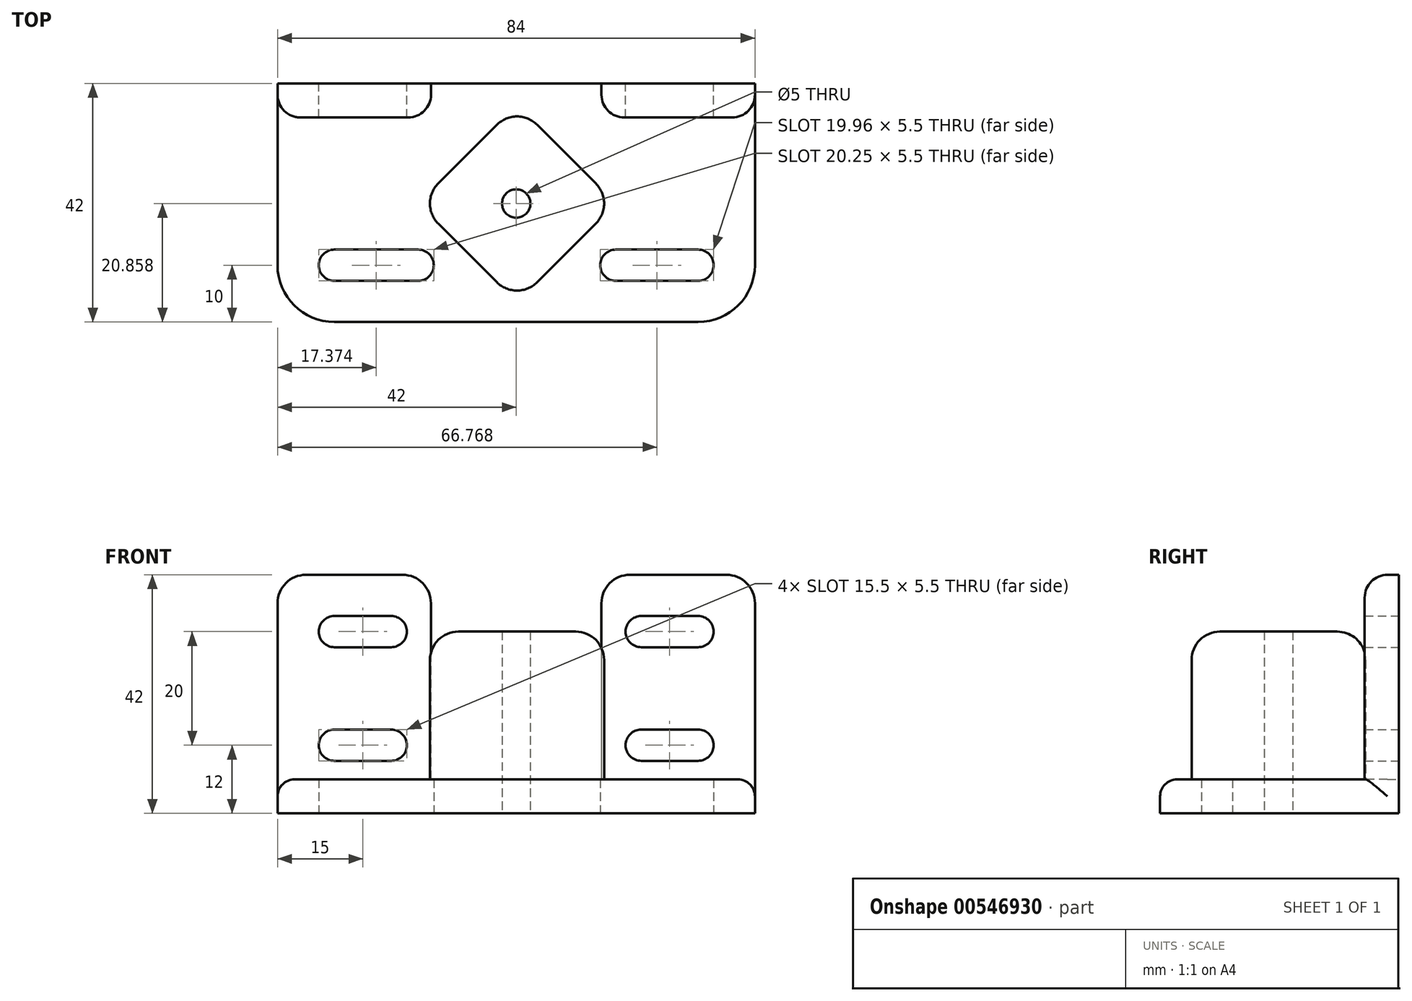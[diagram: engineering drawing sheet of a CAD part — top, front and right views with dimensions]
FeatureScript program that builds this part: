
annotation { "Feature Type Name" : "Feature", "Feature Type Description" : "" }
export const myFeature = defineFeature(function(context is Context, id is Id, definition is map)
    precondition{}
    {
        {
            var Q0;
            Q0=qCreatedBy(makeId("Top.planeOp"),FACE);
            var sketch = newSketch(context, id + "F0", { "sketchPlane" : qUnion([Q0])});
            skLineSegment(sketch, "E0", {"start": v(0, 0) * mm, "end": v(0, -32) * mm});
            skLineSegment(sketch, "E1", {"start": v(10, -42) * mm, "end": v(74, -42) * mm});
            skLineSegment(sketch, "E2", {"start": v(84, -32) * mm, "end": v(84, 0) * mm});
            skLineSegment(sketch, "E3", {"start": v(84, 0) * mm, "end": v(0, 0) * mm});
            skLineSegment(sketch, "E4.0", {"start": v(84.14, -21.14) * mm, "end": v(59.54, -21.14) * mm, "construction": true});
            skLineSegment(sketch, "E5.0", {"start": v(42, 0) * mm, "end": v(42, -42) * mm, "construction": true});
            skLineSegment(sketch, "E6.0", {"start": v(59.54, -21.14) * mm, "end": v(42.14, -3.75) * mm});
            skLineSegment(sketch, "E7.0", {"start": v(42.14, -38.54) * mm, "end": v(24.75, -21.14) * mm});
            skLineSegment(sketch, "E8.0", {"start": v(42.14, -3.75) * mm, "end": v(24.75, -21.14) * mm});
            skLineSegment(sketch, "E9.0", {"start": v(59.54, -21.14) * mm, "end": v(42.14, -38.54) * mm});
            skLineSegment(sketch, "E10.trimOffspring", {"start": v(24.75, -21.14) * mm, "end": v(0.14, -21.14) * mm, "construction": true});
            skLineSegment(sketch, "E11", {"start": v(24.75, 0) * mm, "end": v(24.75, -42) * mm, "construction": true});
            skLineSegment(sketch, "E12", {"start": v(59.54, 0) * mm, "end": v(59.54, -42) * mm, "construction": true});
            skLineSegment(sketch, "E13.0", {"start": v(74, -10) * mm, "end": v(59.54, -10) * mm, "construction": true});
            skLineSegment(sketch, "E14.0", {"start": v(10, -32) * mm, "end": v(24.75, -32) * mm, "construction": true});
            skLineSegment(sketch, "E15.0", {"start": v(10, 0) * mm, "end": v(10, -42) * mm, "construction": true});
            skLineSegment(sketch, "E16.0", {"start": v(74, -42) * mm, "end": v(74, 0) * mm, "construction": true});
            skLineSegment(sketch, "E17.trimOffspring", {"start": v(24.75, -10) * mm, "end": v(10, -10) * mm, "construction": true});
            skLineSegment(sketch, "E18.trimOffspring", {"start": v(59.54, -32) * mm, "end": v(74, -32) * mm, "construction": true});
            skArc(sketch, "E19", {"start": v(10, -29.25) * mm, "mid": v(7.25, -32) * mm, "end": v(10, -34.75) * mm});
            skArc(sketch, "E20", {"start": v(24.75, -34.75) * mm, "mid": v(27.5, -32) * mm, "end": v(24.75, -29.25) * mm});
            skArc(sketch, "E21", {"start": v(59.54, -29.25) * mm, "mid": v(56.79, -32) * mm, "end": v(59.54, -34.75) * mm});
            skArc(sketch, "E22", {"start": v(74, -34.75) * mm, "mid": v(76.75, -32) * mm, "end": v(74, -29.25) * mm});
            skLineSegment(sketch, "E23", {"start": v(10, -29.25) * mm, "end": v(24.75, -29.25) * mm});
            skLineSegment(sketch, "E24", {"start": v(24.75, -34.75) * mm, "end": v(10, -34.75) * mm});
            skLineSegment(sketch, "E25", {"start": v(59.54, -29.25) * mm, "end": v(74, -29.25) * mm});
            skLineSegment(sketch, "E26", {"start": v(74, -34.75) * mm, "end": v(59.54, -34.75) * mm});
            skPoint(sketch, "E27.visualSharp", {"position": v(0, 0) * mm});
            skPoint(sketch, "E28.visualSharp", {"position": v(0, -42) * mm});
            skArc(sketch, "E28.filletArc", {"start": v(0, -32) * mm, "mid": v(2.93, -39.07) * mm, "end": v(10, -42) * mm});
            skPoint(sketch, "E29.visualSharp", {"position": v(84, -42) * mm});
            skArc(sketch, "E29.filletArc", {"start": v(74, -42) * mm, "mid": v(81.07, -39.07) * mm, "end": v(84, -32) * mm});
            skPoint(sketch, "E30.visualSharp", {"position": v(84, 0) * mm});
            skLineSegment(sketch, "E31", {"start": v(24.75, -21.14) * mm, "end": v(42, -21.14) * mm, "construction": true});
            skCircle(sketch, "E32", {"center": v(42, -21.14) * mm, "radius": 2.5 * mm});
            skSolve(sketch);
        }
        {
            var Q0;
            Q0=makeQuery(id+"F0.imprint","IMPRINT",FACE,{"disambiguationData":[TD([[makeQuery(id+"F0.imprint","IMPRINT",EDGE,{"derivedFrom":sQuery(id+"F0.wireOp",EDGE,"E0")}),1.0]])]});
            extrude(context, id + "F1", {"entities" : qUnion([Q0]), "depth" : 6 * mm, "offsetDistance" : 25 * mm});
        }
        {
            var Q0;
            Q0=makeQuery(id+"F0.imprint","IMPRINT",FACE,{"disambiguationData":[TD([[makeQuery(id+"F0.imprint","IMPRINT",EDGE,{"derivedFrom":sQuery(id+"F0.wireOp",EDGE,"E6.0")}),1.0]])]});
            extrude(context, id + "F2", {"entities" : qUnion([Q0]), "operationType" : NewBodyOperationType.ADD, "depth" : 32 * mm, "offsetDistance" : 25 * mm});
        }
        {
            var Q0;
            Q0=makeQuery(id+"F2.opExtrude","SWEPT_EDGE",EDGE,{"disambiguationData":[OSD([sQuery(id+"F0.wireOp",EDGE,"E7.0"),sQuery(id+"F0.wireOp",EDGE,"E9.0")])]});
            var Q1;
            Q1=makeQuery(id+"F2.opExtrude","SWEPT_EDGE",EDGE,{"disambiguationData":[OSD([sQuery(id+"F0.wireOp",EDGE,"E7.0"),sQuery(id+"F0.wireOp",EDGE,"E8.0")])]});
            var Q2;
            Q2=makeQuery(id+"F2.opExtrude","SWEPT_EDGE",EDGE,{"disambiguationData":[OSD([sQuery(id+"F0.wireOp",EDGE,"E6.0"),sQuery(id+"F0.wireOp",EDGE,"E9.0")])]});
            var Q3;
            Q3=makeQuery(id+"F2.opExtrude","SWEPT_EDGE",EDGE,{"disambiguationData":[OSD([sQuery(id+"F0.wireOp",EDGE,"E6.0"),sQuery(id+"F0.wireOp",EDGE,"E8.0")])]});
            var Q4;
            Q4=makeQuery(id+"F2.opExtrude","CAP_EDGE",EDGE,{"disambiguationData":[OSD([sQuery(id+"F0.wireOp",EDGE,"E8.0")])],"isStart":false});
            var Q5;
            Q5=makeQuery(id+"F2.opExtrude","CAP_EDGE",EDGE,{"disambiguationData":[OSD([sQuery(id+"F0.wireOp",EDGE,"E6.0")])],"isStart":false});
            var Q6;
            Q6=makeQuery(id+"F2.opExtrude","CAP_EDGE",EDGE,{"disambiguationData":[OSD([sQuery(id+"F0.wireOp",EDGE,"E9.0")])],"isStart":false});
            var Q7;
            Q7=makeQuery(id+"F2.opExtrude","CAP_EDGE",EDGE,{"disambiguationData":[OSD([sQuery(id+"F0.wireOp",EDGE,"E7.0")])],"isStart":false});
            fillet(context, id + "F3", {"entities" : qUnion([Q0, Q1, Q2, Q3, Q4, Q5, Q6, Q7]), "radius" : 5 * mm, "tangentPropagation" : true, "allowEdgeOverflow" : false});
        }
        {
            var Q0;
            Q0=makeQuery(id+"F1.opExtrude","CAP_EDGE",EDGE,{"disambiguationData":[OSD([sQuery(id+"F0.wireOp",EDGE,"E1")])],"isStart":false});
            fillet(context, id + "F4", {"entities" : qUnion([Q0]), "radius" : 3 * mm, "tangentPropagation" : true, "allowEdgeOverflow" : false});
        }
        {
            var Q0;
            Q0=qCreatedBy(makeId("Front.planeOp"),FACE);
            var sketch = newSketch(context, id + "F5", { "sketchPlane" : qUnion([Q0])});
            skLineSegment(sketch, "E33", {"start": v(0, 0) * mm, "end": v(0, 37) * mm});
            skLineSegment(sketch, "E34", {"start": v(5, 42) * mm, "end": v(22, 42) * mm});
            skLineSegment(sketch, "E35", {"start": v(84, 37) * mm, "end": v(84, 0) * mm});
            skLineSegment(sketch, "E36.0", {"start": v(10, 32) * mm, "end": v(20, 32) * mm, "construction": true});
            skLineSegment(sketch, "E37.0", {"start": v(10, 9.25) * mm, "end": v(10, 14.75) * mm, "construction": true});
            skLineSegment(sketch, "E38.0", {"start": v(74, 34.75) * mm, "end": v(74, 29.25) * mm, "construction": true});
            skLineSegment(sketch, "E39.0", {"start": v(20, 9.25) * mm, "end": v(20, 14.75) * mm, "construction": true});
            skLineSegment(sketch, "E40.0", {"start": v(64, 34.75) * mm, "end": v(64, 29.25) * mm, "construction": true});
            skLineSegment(sketch, "E41.trimOffspring", {"start": v(62, 42) * mm, "end": v(79, 42) * mm});
            skPoint(sketch, "E42.visualSharp", {"position": v(0, 42) * mm});
            skArc(sketch, "E42.filletArc", {"start": v(5, 42) * mm, "mid": v(1.46, 40.54) * mm, "end": v(0, 37) * mm});
            skPoint(sketch, "E43.visualSharp", {"position": v(84, 42) * mm});
            skArc(sketch, "E43.filletArc", {"start": v(84, 37) * mm, "mid": v(82.54, 40.54) * mm, "end": v(79, 42) * mm});
            skLineSegment(sketch, "E44.trimOffspring", {"start": v(64, 32) * mm, "end": v(74, 32) * mm, "construction": true});
            skArc(sketch, "E45", {"start": v(20, 29.25) * mm, "mid": v(22.75, 32) * mm, "end": v(20, 34.75) * mm});
            skArc(sketch, "E46", {"start": v(10, 34.75) * mm, "mid": v(7.25, 32) * mm, "end": v(10, 29.25) * mm});
            skArc(sketch, "E47", {"start": v(64, 34.75) * mm, "mid": v(61.25, 32) * mm, "end": v(64, 29.25) * mm});
            skArc(sketch, "E48", {"start": v(74, 29.25) * mm, "mid": v(76.75, 32) * mm, "end": v(74, 34.75) * mm});
            skLineSegment(sketch, "E49.0", {"start": v(10, 12) * mm, "end": v(20, 12) * mm, "construction": true});
            skLineSegment(sketch, "E50.0", {"start": v(64, 12) * mm, "end": v(74, 12) * mm, "construction": true});
            skArc(sketch, "E51", {"start": v(10, 14.75) * mm, "mid": v(7.25, 12) * mm, "end": v(10, 9.25) * mm});
            skArc(sketch, "E52", {"start": v(20, 9.25) * mm, "mid": v(22.75, 12) * mm, "end": v(20, 14.75) * mm});
            skArc(sketch, "E53", {"start": v(64, 14.75) * mm, "mid": v(61.25, 12) * mm, "end": v(64, 9.25) * mm});
            skArc(sketch, "E54", {"start": v(74, 9.25) * mm, "mid": v(76.75, 12) * mm, "end": v(74, 14.75) * mm});
            skLineSegment(sketch, "E55", {"start": v(0, 0) * mm, "end": v(27, 0) * mm});
            skLineSegment(sketch, "E56", {"start": v(57, 0) * mm, "end": v(84, 0) * mm});
            skLineSegment(sketch, "E57.trimOffspring", {"start": v(10, 29.25) * mm, "end": v(10, 34.75) * mm, "construction": true});
            skLineSegment(sketch, "E58.trimOffspring", {"start": v(20, 29.25) * mm, "end": v(20, 34.75) * mm, "construction": true});
            skLineSegment(sketch, "E59.trimOffspring", {"start": v(64, 14.75) * mm, "end": v(64, 9.25) * mm, "construction": true});
            skLineSegment(sketch, "E60.trimOffspring", {"start": v(74, 14.75) * mm, "end": v(74, 9.25) * mm, "construction": true});
            skLineSegment(sketch, "E61", {"start": v(10, 34.75) * mm, "end": v(20, 34.75) * mm});
            skLineSegment(sketch, "E62", {"start": v(10, 29.25) * mm, "end": v(20, 29.25) * mm});
            skLineSegment(sketch, "E63", {"start": v(10, 14.75) * mm, "end": v(20, 14.75) * mm});
            skLineSegment(sketch, "E64", {"start": v(10, 9.25) * mm, "end": v(20, 9.25) * mm});
            skLineSegment(sketch, "E65", {"start": v(64, 34.75) * mm, "end": v(74, 34.75) * mm});
            skLineSegment(sketch, "E66", {"start": v(74, 29.25) * mm, "end": v(64, 29.25) * mm});
            skLineSegment(sketch, "E67", {"start": v(74, 14.75) * mm, "end": v(64, 14.75) * mm});
            skLineSegment(sketch, "E68", {"start": v(64, 9.25) * mm, "end": v(74, 9.25) * mm});
            skLineSegment(sketch, "E69.0", {"start": v(27, 0) * mm, "end": v(27, 37) * mm});
            skLineSegment(sketch, "E70.0", {"start": v(57, 37) * mm, "end": v(57, 0) * mm});
            skPoint(sketch, "E71.visualSharp", {"position": v(27, 42) * mm});
            skArc(sketch, "E71.filletArc", {"start": v(27, 37) * mm, "mid": v(25.54, 40.54) * mm, "end": v(22, 42) * mm});
            skPoint(sketch, "E72.visualSharp", {"position": v(57, 42) * mm});
            skArc(sketch, "E72.filletArc", {"start": v(62, 42) * mm, "mid": v(58.46, 40.54) * mm, "end": v(57, 37) * mm});
            skSolve(sketch);
        }
        {
            var Q0;
            Q0=makeQuery(id+"F5.imprint","IMPRINT",FACE,{"disambiguationData":[TD([[makeQuery(id+"F5.imprint","IMPRINT",EDGE,{"derivedFrom":sQuery(id+"F5.wireOp",EDGE,"E33")}),-1.0]])]});
            var Q1;
            Q1=makeQuery(id+"F5.imprint","IMPRINT",FACE,{"disambiguationData":[TD([[makeQuery(id+"F5.imprint","IMPRINT",EDGE,{"derivedFrom":sQuery(id+"F5.wireOp",EDGE,"E35")}),-1.0]])]});
            extrude(context, id + "F6", {"entities" : qUnion([Q0, Q1]), "operationType" : NewBodyOperationType.ADD, "depth" : 6 * mm, "offsetDistance" : 25 * mm});
        }
        {
            var Q0;
            Q0=makeQuery(id+"F6.opExtrude","CAP_EDGE",EDGE,{"disambiguationData":[OSD([sQuery(id+"F5.wireOp",EDGE,"E33")])],"isStart":false});
            var Q1;
            Q1=makeQuery(id+"F6.opExtrude","CAP_EDGE",EDGE,{"disambiguationData":[OSD([sQuery(id+"F5.wireOp",EDGE,"E35")])],"isStart":false});
            fillet(context, id + "F7", {"entities" : qUnion([Q0, Q1]), "radius" : 4 * mm, "tangentPropagation" : true, "allowEdgeOverflow" : false});
        }
    });
